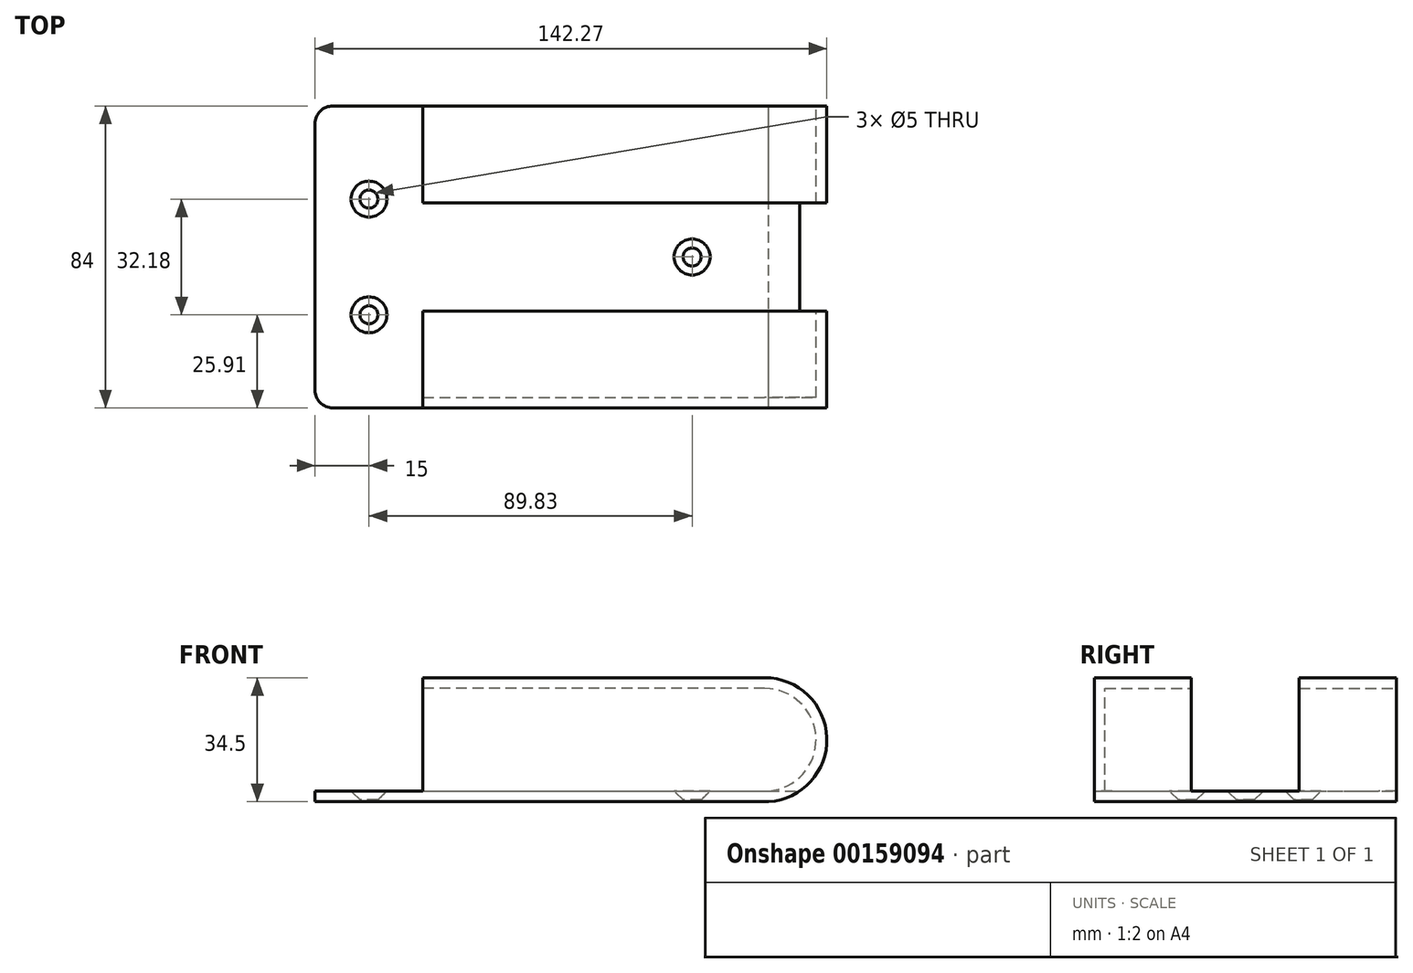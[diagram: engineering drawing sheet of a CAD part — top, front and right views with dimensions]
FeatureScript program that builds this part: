
annotation { "Feature Type Name" : "Feature", "Feature Type Description" : "" }
export const myFeature = defineFeature(function(context is Context, id is Id, definition is map)
    precondition{}
    {
        {
            var Q0;
            Q0=qCreatedBy(makeId("Front.planeOp"),FACE);
            var sketch = newSketch(context, id + "F0", { "sketchPlane" : qUnion([Q0])});
            skLineSegment(sketch, "E0", {"start": v(-74.83, 14.25) * mm, "end": v(20.17, 14.25) * mm});
            skLineSegment(sketch, "E1", {"start": v(-104.83, -14.25) * mm, "end": v(21.2, -14.25) * mm});
            skArc(sketch, "E2", {"start": v(21.2, -14.25) * mm, "mid": v(34.43, 0.5) * mm, "end": v(20.17, 14.25) * mm});
            skLineSegment(sketch, "E3", {"start": v(-49.29, 28.8) * mm, "end": v(-49.29, -26.5) * mm, "construction": true});
            skLineSegment(sketch, "E4.0", {"start": v(-74.83, 17.25) * mm, "end": v(20.17, 17.25) * mm});
            skArc(sketch, "E4.1", {"start": v(21.3, -17.25) * mm, "mid": v(37.43, 0.55) * mm, "end": v(20.17, 17.25) * mm});
            skLineSegment(sketch, "E4.2", {"start": v(-104.83, -17.25) * mm, "end": v(21.3, -17.25) * mm});
            skLineSegment(sketch, "E5", {"start": v(-74.83, 14.25) * mm, "end": v(-74.83, 17.25) * mm});
            skLineSegment(sketch, "E6", {"start": v(-104.83, -17.25) * mm, "end": v(-104.83, -14.25) * mm});
            skSolve(sketch);
        }
        {
            var Q0;
            Q0 = qSketchRegion(id + "F0", true);
            extrude(context, id + "F1", {"entities" : qUnion([Q0]), "depth" : 42 * mm, "hasSecondDirection" : true, "secondDirectionOppositeDirection" : true, "secondDirectionDepth" : 42 * mm});
        }
        {
            var Q0;
            Q0=makeQuery(id+"F1.opExtrude","CAP_FACE",FACE,{"disambiguationData":[OSD([sQuery(id+"F0.wireOp",EDGE,"E0"),sQuery(id+"F0.wireOp",EDGE,"E1"),sQuery(id+"F0.wireOp",EDGE,"E2"),sQuery(id+"F0.wireOp",EDGE,"E4.0"),sQuery(id+"F0.wireOp",EDGE,"E4.1"),sQuery(id+"F0.wireOp",EDGE,"E4.2"),sQuery(id+"F0.wireOp",EDGE,"E5"),sQuery(id+"F0.wireOp",EDGE,"E6")])],"isStart":false});
            var sketch = newSketch(context, id + "F2", { "sketchPlane" : qUnion([Q0])});
            skLineSegment(sketch, "E7.0", {"start": v(-74.83, 17.25) * mm, "end": v(20.17, 17.25) * mm});
            skArc(sketch, "E7.1", {"start": v(21.3, -17.25) * mm, "mid": v(37.43, 0.55) * mm, "end": v(20.17, 17.25) * mm});
            skLineSegment(sketch, "E8", {"start": v(21.3, -17.25) * mm, "end": v(-74.83, -17.25) * mm});
            skLineSegment(sketch, "E9", {"start": v(-74.83, 17.25) * mm, "end": v(-74.83, -27.98) * mm, "construction": true});
            skLineSegment(sketch, "E10", {"start": v(-74.83, -17.25) * mm, "end": v(-74.83, 17.25) * mm});
            skSolve(sketch);
        }
        {
            var Q0;
            Q0 = qSketchRegion(id + "F2", true);
            extrude(context, id + "F3", {"entities" : qUnion([Q0]), "operationType" : NewBodyOperationType.ADD, "oppositeDirection" : true, "depth" : 3 * mm});
        }
        {
            var Q0;
            Q0=makeQuery(id+"F1.opExtrude","SWEPT_FACE",FACE,{"disambiguationData":[OSD([sQuery(id+"F0.wireOp",EDGE,"E1")])]});
            var sketch = newSketch(context, id + "F4", { "sketchPlane" : qUnion([Q0])});
            skLineSegment(sketch, "E11.bottom", {"start": v(-105.53, -15) * mm, "end": v(65.54, -15) * mm});
            skLineSegment(sketch, "E11.top", {"start": v(-105.53, 15) * mm, "end": v(65.54, 15) * mm});
            skLineSegment(sketch, "E11.left", {"start": v(-105.53, -15) * mm, "end": v(-105.53, 15) * mm});
            skLineSegment(sketch, "E11.right", {"start": v(65.54, -15) * mm, "end": v(65.54, 15) * mm});
            skSolve(sketch);
        }
        {
            var Q0;
            Q0 = qSketchRegion(id + "F4", true);
            extrude(context, id + "F5", {"entities" : qUnion([Q0]), "operationType" : NewBodyOperationType.REMOVE, "endBound" : BoundingType.THROUGH_ALL, "depth" : 25 * mm});
        }
        {
            var Q0;
            Q0=makeQuery(id+"F1.opExtrude","CAP_EDGE",EDGE,{"disambiguationData":[OSD([sQuery(id+"F0.wireOp",EDGE,"E6")])],"isStart":false});
            var Q1;
            Q1=makeQuery(id+"F1.opExtrude","CAP_EDGE",EDGE,{"disambiguationData":[OSD([sQuery(id+"F0.wireOp",EDGE,"E6")])],"isStart":true});
            fillet(context, id + "F6", {"entities" : qUnion([Q0, Q1]), "radius" : 5 * mm, "tangentPropagation" : true, "allowEdgeOverflow" : false});
        }
        {
            var Q0;
            Q0=makeQuery(id+"F5.boolean.opBoolean","MERGE",FACE,{"derivedFrom":[makeQuery(id+"F1.opExtrude","SWEPT_FACE",FACE,{"disambiguationData":[OSD([sQuery(id+"F0.wireOp",EDGE,"E1")])]}),makeQuery(id+"F5.opExtrude","CAP_FACE",FACE,{"disambiguationData":[OSD([sQuery(id+"F4.wireOp",EDGE,"E11.bottom"),sQuery(id+"F4.wireOp",EDGE,"E11.top"),sQuery(id+"F4.wireOp",EDGE,"E11.left"),sQuery(id+"F4.wireOp",EDGE,"E11.right")])],"isStart":true})]});
            var sketch = newSketch(context, id + "F7", { "sketchPlane" : qUnion([Q0])});
            skPoint(sketch, "E12", {"position": v(0, 0) * mm});
            skPoint(sketch, "E13", {"position": v(-89.83, -16.1) * mm});
            skPoint(sketch, "E14", {"position": v(-89.83, 16.1) * mm});
            skLineSegment(sketch, "E15", {"start": v(-89.83, -49.21) * mm, "end": v(-89.83, 50.15) * mm, "construction": true});
            skSolve(sketch);
        }
        {
            var Q0;
            Q0=sQuery(id+"F7.wireOp",VERTEX,"E13");
            var Q1;
            Q1=sQuery(id+"F7.wireOp",VERTEX,"E14");
            var Q2;
            Q2=sQuery(id+"F7.wireOp",VERTEX,"E12");
            var Q3;
            Q3=makeQuery(id+"F1.opExtrude","SWEPT_BODY",BODY,{"disambiguationData":[OSD([sQuery(id+"F0.wireOp",EDGE,"E0"),sQuery(id+"F0.wireOp",EDGE,"E1"),sQuery(id+"F0.wireOp",EDGE,"E2"),sQuery(id+"F0.wireOp",EDGE,"E4.0"),sQuery(id+"F0.wireOp",EDGE,"E4.1"),sQuery(id+"F0.wireOp",EDGE,"E4.2"),sQuery(id+"F0.wireOp",EDGE,"E5"),sQuery(id+"F0.wireOp",EDGE,"E6")])]});
            hole(context, id + "F8", {"style" : HoleStyle.C_SINK, "endStyle" : HoleEndStyle.THROUGH, "holeDiameter" : 5 * mm, "cSinkDiameter" : 10 * mm, "cSinkAngle" : 90 * degree, "locations" : qUnion([Q0, Q1, Q2]), "scope" : qUnion([Q3]), "isTappedThrough" : true});
        }
    });
